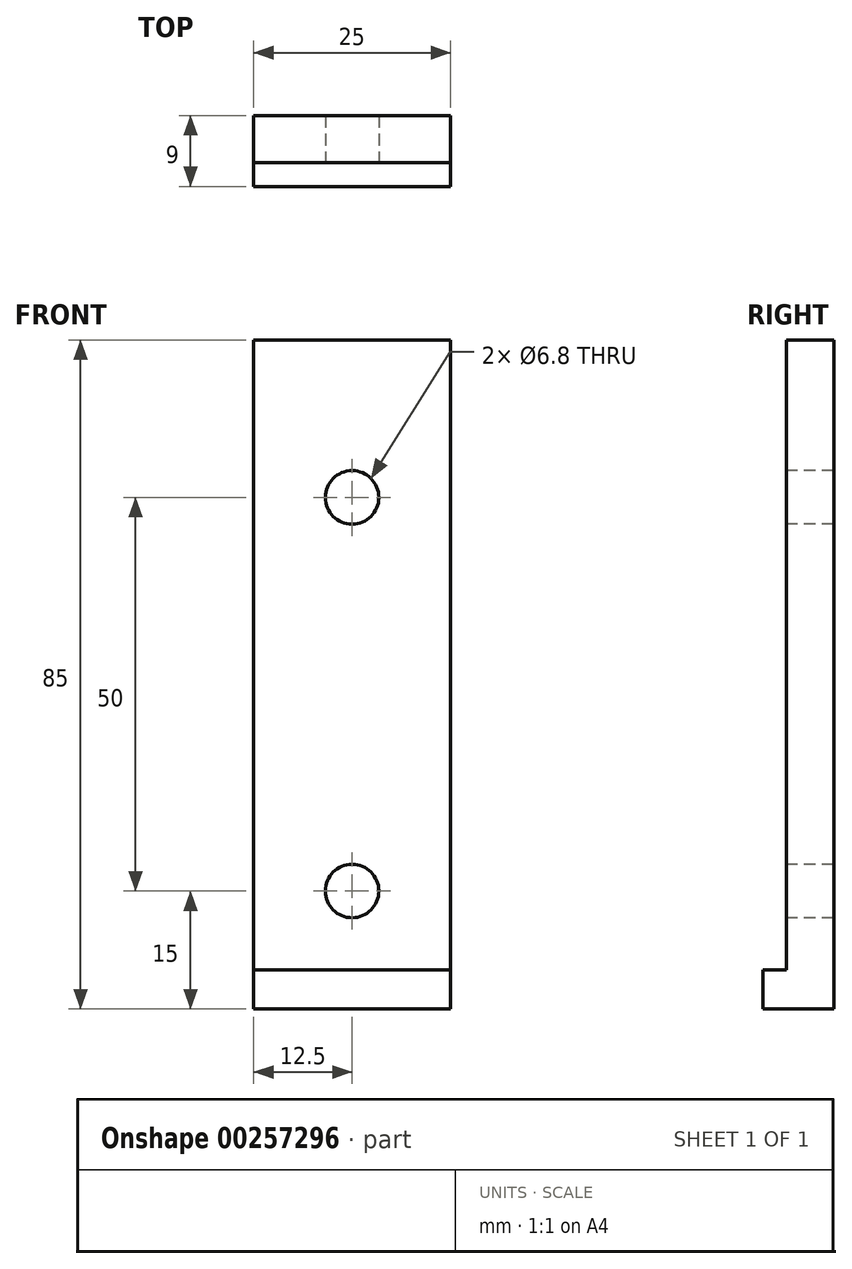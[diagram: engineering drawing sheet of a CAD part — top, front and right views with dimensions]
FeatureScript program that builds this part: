
annotation { "Feature Type Name" : "Feature", "Feature Type Description" : "" }
export const myFeature = defineFeature(function(context is Context, id is Id, definition is map)
    precondition{}
    {
        {
            var Q0;
            Q0=qCreatedBy(makeId("Right.planeOp"),FACE);
            var sketch = newSketch(context, id + "F0", { "sketchPlane" : qUnion([Q0])});
            skLineSegment(sketch, "E0", {"start": v(0, 85) * mm, "end": v(0, 0) * mm});
            skLineSegment(sketch, "E1", {"start": v(0, 0) * mm, "end": v(-9, 0) * mm});
            skLineSegment(sketch, "E2", {"start": v(-9, 0) * mm, "end": v(-9, 5) * mm});
            skLineSegment(sketch, "E3", {"start": v(-9, 5) * mm, "end": v(-6, 5) * mm});
            skLineSegment(sketch, "E4", {"start": v(-6, 5) * mm, "end": v(-6, 85) * mm});
            skLineSegment(sketch, "E5", {"start": v(-6, 85) * mm, "end": v(0, 85) * mm});
            skSolve(sketch);
        }
        {
            var Q0;
            Q0=makeQuery(id+"F0.imprint","IMPRINT",FACE,{"disambiguationData":[TD([[makeQuery(id+"F0.imprint","IMPRINT",EDGE,{"derivedFrom":sQuery(id+"F0.wireOp",EDGE,"E0")}),-1.0]])]});
            extrude(context, id + "F1", {"entities" : qUnion([Q0]), "oppositeDirection" : true, "depth" : 25 * mm});
        }
        {
            var Q0;
            Q0=makeQuery(id+"F1.opExtrude","SWEPT_FACE",FACE,{"disambiguationData":[OSD([sQuery(id+"F0.wireOp",EDGE,"E4")])]});
            var sketch = newSketch(context, id + "F2", { "sketchPlane" : qUnion([Q0])});
            skPoint(sketch, "E6", {"position": v(-12.5, 15) * mm});
            skPoint(sketch, "E7", {"position": v(-12.5, 65) * mm});
            skSolve(sketch);
        }
        {
            var Q0;
            Q0=sQuery(id+"F2.wireOp",VERTEX,"E7");
            var Q1;
            Q1=sQuery(id+"F2.wireOp",VERTEX,"E6");
            var Q2;
            Q2=makeQuery(id+"F1.opExtrude","SWEPT_BODY",BODY,{"disambiguationData":[OSD([sQuery(id+"F0.wireOp",EDGE,"E0"),sQuery(id+"F0.wireOp",EDGE,"E1"),sQuery(id+"F0.wireOp",EDGE,"E2"),sQuery(id+"F0.wireOp",EDGE,"E3"),sQuery(id+"F0.wireOp",EDGE,"E4"),sQuery(id+"F0.wireOp",EDGE,"E5")])]});
            hole(context, id + "F3", {"style" : HoleStyle.SIMPLE, "endStyle" : HoleEndStyle.THROUGH, "standardTappedOrClearance" : lookupTablePath({ "standard" : "ISO", "fit" : "Normal", "engagement" : "75%", "pitch" : "1.25 mm", "size" : "M8", "type" : "Tapped" }), "standardBlindInLast" : lookupTablePath({ "fit" : "Standard", "standard" : "ISO", "engagement" : "75%", "pitch" : "1.25 mm", "size" : "M8", "type" : "Tapped" }), "holeDiameter" : 6.8 * mm, "showTappedDepth" : true, "tappedDepth" : 12 * mm, "tapClearance" : 3, "locations" : qUnion([Q0, Q1]), "scope" : qUnion([Q2]), "majorDiameter" : 8 * mm});
        }
    });
